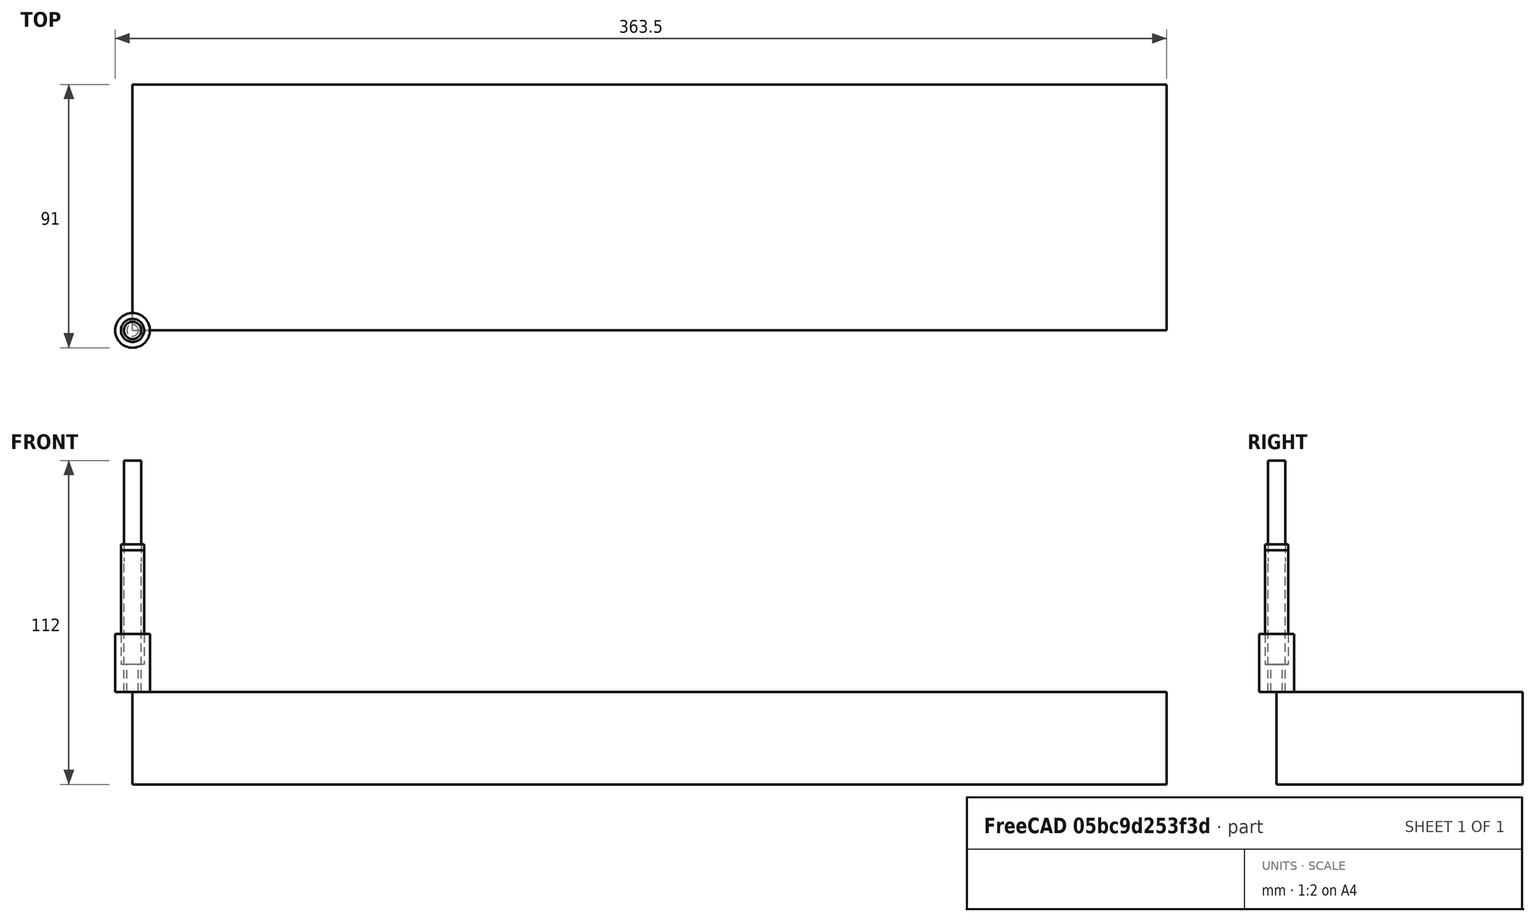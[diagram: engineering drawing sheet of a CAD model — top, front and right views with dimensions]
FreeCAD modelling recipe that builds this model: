
FCSTD DOCUMENT  (FreeCAD 0.22R34789 (Git))
Label: fence_side
License: All rights reserved
LicenseURL: http://en.wikipedia.org/wiki/All_rights_reserved
objects: Path::FeaturePython×8, Part::FeaturePython×5, Sketcher::SketchObject×4, PartDesign::Pocket×3, App::DocumentObjectGroup×3, PartDesign::Pad×1, PartDesign::Body×1, Spreadsheet::Sheet×1, App::FeaturePython×1, Mesh::FeaturePython×1
note: 21 computed .brp shape members not serialized (recipe doc carries the construction recipe); baked Part::Feature solids carry a one-line shape summary decoded from their .brp

FEATURE [Sketcher::SketchObject] Sketch012  label="fence_face"
  FullyConstrained = true
  MapMode = 5
  Support = -> [XY_Plane005]
  expr: .Constraints.fence_length = Spreadsheet.table_length / 2 - 45 / 2
  expr: Constraints[11] = 3 * Spreadsheet.table_radius
  sketch-geometry (6):
    g0: LineSegment StartX=18 StartY=65 StartZ=0 EndX=319.5 EndY=65 EndZ=0
    g1: LineSegment StartX=337.5 StartY=47 StartZ=0 EndX=337.5 EndY=0 EndZ=0
    g2: LineSegment StartX=337.5 StartY=0 StartZ=0 EndX=0 EndY=0 EndZ=0
    g3: LineSegment StartX=0 StartY=0 StartZ=0 EndX=0 EndY=47 EndZ=0
    g4: ArcOfCircle CenterX=18 CenterY=47 CenterZ=0 NormalX=0 NormalY=0 NormalZ=1 AngleXU=0 Radius=18 StartAngle=1.5708 EndAngle=3.14159
    g5: ArcOfCircle CenterX=319.5 CenterY=47 CenterZ=0 NormalX=0 NormalY=0 NormalZ=1 AngleXU=0 Radius=18 StartAngle=2e-16 EndAngle=1.5708
  constraints (15):
    c: Coincident(g1,g2)
    c: Coincident(g2,g3)
    c: Horizontal(g0)
    c: Horizontal(g2)
    c: Vertical(g1)
    c: Vertical(g3)
    c: Tangent(g3,g4) = 1.5708
    c: Tangent(g0,g4) = 1.5708
    c: Tangent(g0,g5) = 1.5708
    c: Tangent(g1,g5) = 1.5708
    c: Equal(g4,g5)
    c: Radius(g4) = 18
    c: DistanceX(g2,g2) = 337.5  'fence_length'
    c: Coincident(g2,g-1)
    c: DistanceY(g1,g0) = 65  'fence_height'
FEATURE [PartDesign::Pad] Pad005
  Direction = (0,0,1)
  Length = 32
  Length2 = 10
  Profile = -> Sketch012
  ReferenceAxis = -> Sketch012 [N_Axis]
  Type = 0
  expr: Length = Spreadsheet.fence_face_d
FEATURE [Sketcher::SketchObject] Sketch013
  FullyConstrained = true
  MapMode = 5
  Placement = pos=(0,0,32) rot=(0,0,1;0rad)
  Support = -> [Pad005]
  expr: Constraints[11] = Sketch012.Constraints.fence_height / 2 - 9.5 mm + 3 mm
  expr: Constraints[8] = Spreadsheet.t_track_width
  expr: Constraints[9] = Sketch012.Constraints.fence_length
  sketch-geometry (4):
    g0: LineSegment StartX=0 StartY=45 StartZ=0 EndX=337.5 EndY=45 EndZ=0
    g1: LineSegment StartX=337.5 StartY=45 StartZ=0 EndX=337.5 EndY=26 EndZ=0
    g2: LineSegment StartX=337.5 StartY=26 StartZ=0 EndX=0 EndY=26 EndZ=0
    g3: LineSegment StartX=0 StartY=26 StartZ=0 EndX=0 EndY=45 EndZ=0
  constraints (12):
    c: Coincident(g0,g1)
    c: Coincident(g1,g2)
    c: Coincident(g2,g3)
    c: Coincident(g3,g0)
    c: Horizontal(g0)
    c: Horizontal(g2)
    c: Vertical(g1)
    c: Vertical(g3)
    c: DistanceY(g3,g3) = 19
    c: DistanceX(g2,g2) = 337.5
    c: DistanceX(g2,g-1) = 0
    c: DistanceY(g-1,g2) = 26
FEATURE [PartDesign::Pocket] Pocket007
  BaseFeature = -> Pad005
  Direction = (0,0,-1)
  Length = 9.5
  Length2 = 5
  Profile = -> Sketch013
  ReferenceAxis = -> Sketch013 [N_Axis]
  Type = 0
  expr: Length = Spreadsheet.t_track_depth
FEATURE [Sketcher::SketchObject] Sketch014
  FullyConstrained = true
  MapMode = 5
  Placement = pos=(0,0,32) rot=(0,0,1;0rad)
  Support = -> [Pocket007]
  expr: Constraints[10] = Sketch012.Constraints.fence_length
  sketch-geometry (4):
    g0: LineSegment StartX=0 StartY=4 StartZ=0 EndX=337.5 EndY=4 EndZ=0
    g1: LineSegment StartX=337.5 StartY=4 StartZ=0 EndX=337.5 EndY=0 EndZ=0
    g2: LineSegment StartX=337.5 StartY=0 StartZ=0 EndX=0 EndY=0 EndZ=0
    g3: LineSegment StartX=0 StartY=0 StartZ=0 EndX=0 EndY=4 EndZ=0
  constraints (11):
    c: Coincident(g0,g1)
    c: Coincident(g1,g2)
    c: Coincident(g2,g3)
    c: Coincident(g3,g0)
    c: Horizontal(g0)
    c: Horizontal(g2)
    c: Vertical(g1)
    c: Vertical(g3)
    c: DistanceY(g1,g1) = 4
    c: Coincident(g2,g-1)
    c: DistanceX(g2,g2) = 337.5
FEATURE [PartDesign::Pocket] Pocket008
  BaseFeature = -> Pocket007
  Direction = (0,0,-1)
  Length = 4
  Length2 = 5
  Profile = -> Sketch014
  ReferenceAxis = -> Sketch014 [N_Axis]
  Type = 0
FEATURE [Sketcher::SketchObject] Sketch015
  FullyConstrained = true
  MapMode = 5
  Placement = pos=(0,0,0) rot=(1,0,0;3.14159rad)
  Support = -> [Pocket008]
  expr: Constraints[8] = Spreadsheet.fence_base_d
  expr: Constraints[9] = Sketch012.Constraints.fence_length
  sketch-geometry (4):
    g0: LineSegment StartX=0 StartY=0 StartZ=0 EndX=337.5 EndY=0 EndZ=0
    g1: LineSegment StartX=337.5 StartY=0 StartZ=0 EndX=337.5 EndY=-32 EndZ=0
    g2: LineSegment StartX=337.5 StartY=-32 StartZ=0 EndX=0 EndY=-32 EndZ=0
    g3: LineSegment StartX=0 StartY=-32 StartZ=0 EndX=0 EndY=0 EndZ=0
  constraints (11):
    c: Coincident(g0,g1)
    c: Coincident(g1,g2)
    c: Coincident(g2,g3)
    c: Coincident(g3,g0)
    c: Horizontal(g0)
    c: Horizontal(g2)
    c: Vertical(g1)
    c: Vertical(g3)
    c: DistanceY(g1,g1) = 32
    c: DistanceX(g0,g0) = 337.5
    c: Coincident(g-1,g0)
FEATURE [PartDesign::Pocket] Pocket009
  BaseFeature = -> Pocket008
  Direction = (0,0,1)
  Length = 6
  Length2 = 5
  Profile = -> Sketch015
  ReferenceAxis = -> Sketch015 [N_Axis]
  Type = 0
FEATURE [PartDesign::Body] Body004  label="fence_face_r"
  Group = -> [Sketch012,Pad005,Sketch013,Pocket007,Sketch014,Pocket008,Sketch015,Pocket009]
  Origin = -> Origin004
  Tip = -> Pocket009
FEATURE [Spreadsheet::Sheet] Spreadsheet
  cells = A1='table_length; B1(table_length)=720; D1='plywood_18; E1(ply_18)=18; F1='iron_cast_table; G1(iron_cast_table)=262; I1='nakrętka kłowa M8 DIN1624; L1='otwory_przelotowe; A2='table_depth; B2(table_depth)=420; D2='plywood_12; E2(ply_12)=12; F2='mounting_screws_distance; G2(mounting_screws_distance)=170; I2='M8_D; J2(DIN1624_M8_D)=22.2; L2='M8_D; M2(otw_przel_M8)=8.4; D3='plywood_3; E3(ply_3)=3; I3='M8_d1; J3(DIN1624_M8_d1)=9.1; A4='table_radius; B4(table_radius)=6; I4='M8_a; J4(DIN1624_M8_a)=1.2; I5='M8_L1; J5(DIN1624_M8_L1)=11; A6='t_track_slim_width; B6(t_track_width)=19; C6='https://allegro.pl/oferta/t-track-slim-1220mm-profil-aluminiowy-t-zielony-10608302634?fromVariant=12640372726; A7='t_track_slim_depth; B7(t_track_depth)=9.5; D7='fence_base_d; E7(fence_base_d)=32; I7='M10_D; J7(DIN1624_M10_D)=25.5; D8='fence_face_d; E8(fence_face_d)=32; I8='M10_d1; J8(DIN1624_M10_d1)=12; A9='clamp_slot_width; B9(clamp_slot_width)=32; I9='M10_a; J9(DIN1624_M10_a)=1.2; I10='M10_L1; J10(DIN1624_M10_L1)=13; A11='insert_width; B11(insert_width)=90; D11='base_width; E11(base_width)==G1; A12='insert_depth; B12(insert_depth)=200; D12='base_depth; E12(base_depth)==E1 + 60 + E2 + E15 + 10; I12='M12_D; J12(DIN1624_M12_D)=27; D13='base_height; E13(base_height)=75; I13='M12_d1; J13(DIN1624_M12_d1)=13.7; I14='M12_a; J14(DIN1624_M12_a)=1.6; D15='drawer_depth; E15(drawer_depth)=200; I15='M12_L1; J15(DIN1624_M12_L1)=14.5; D16='drawer_slide_width; E16=12.7; D17='drawer_total_depth; E17(drawer_total_depth)==E15 + 6; D18='drawer_total_width; E18(drawer_total_width)==E11 - 2 * E1 - 2 * E16; D19='drawer_total_height; E19(drawer_total_height)==E13 - E1 - 9
FEATURE [App::FeaturePython] SetupSheet  # Path/CAM operation (typed FeaturePython)
  ClearanceHeightExpression = OpStockZMax+SetupSheet.ClearanceHeightOffset
  ClearanceHeightOffset = 5
  CoolantMode = 0
  CoolantModes = None | Flood | Mist
  FinalDepthExpression = OpFinalDepth
  HorizRapid = 0
  SafeHeightExpression = OpStockZMax+SetupSheet.SafeHeightOffset
  SafeHeightOffset = 3
  StartDepthExpression = OpStartDepth
  StepDownExpression = OpToolDiameter
  VertRapid = 0
FEATURE [Part::FeaturePython] Clone  label="Model-fence_face_r"  # Draft clone (typed FeaturePython)
  AttacherType = Attacher::AttachEngine3D
  Fuse = false
  Objects = -> [Body004]
  PathResource = Model
  Placement = pos=(10,10,-32) rot=(1,0,0;0rad)
  Scale = (1,1,1)
FEATURE [App::DocumentObjectGroup] Model
  Group = -> [Clone]
FEATURE [Part::FeaturePython] Stock  # WARN: FeaturePython — macro-defined, semantics opaque (R4)
  Base = -> Model
  ExtXneg = 10
  ExtXpos = 10
  ExtYneg = 10
  ExtYpos = 10
  ExtZneg = 0
  ExtZpos = 0
  Placement = pos=(10,10,-32) rot=(0,0,1;0rad)
  StockType = FromBase
FEATURE [Part::FeaturePython] ToolBit001  label="6 mm endmill, D=6, H=45, L=80, S=6"  # Path/CAM toolbit (typed FeaturePython)
  BitPropertyNames = Chipload | CuttingEdgeHeight | Diameter | Flutes | Length | Material | ShankDiameter | SpindleDirection
  BitShape = <userpath>/.local/share/FreeCAD/Macro/Tools/Shape/endmill.fcstd
  Chipload = 0
  CuttingEdgeHeight = 45
  Diameter = 6
  File = <userpath>/.local/share/FreeCAD/Macro/Tools/Bit/03c10998-7ce6-11ee-8713-1065300da2fe.fctb
  Flutes = 2
  Length = 80
  Material = 1
  ShankDiameter = 6
  ShapeName = endmill
  SpindleDirection = 0
FEATURE [Path::FeaturePython] TC__6_mm_endmill__D_6__H_45__L_80__S_6  label="TC: 6 mm endmill, D=6, H=45, L=80, S=6"  # Path/CAM operation (typed FeaturePython)
  HorizFeed = 10
  HorizRapid = 0
  SpindleDir = 0
  SpindleSpeed = 0
  Tool = -> ToolBit001
  ToolNumber = 17
  VertFeed = 1
  VertRapid = 0
  expr: HorizRapid = SetupSheet.HorizRapid
  expr: VertRapid = SetupSheet.VertRapid
FEATURE [Part::FeaturePython] endmill_D_4__h_9_5__S_8  label="endmill D=4, h=9.5, S=8"  # Path/CAM toolbit (typed FeaturePython)
  BitPropertyNames = Chipload | CuttingEdgeHeight | Diameter | Flutes | Length | Material | ShankDiameter | SpindleDirection
  BitShape = <userpath>/.local/share/FreeCAD/Macro/Tools/Shape/endmill.fcstd
  Chipload = 0
  CuttingEdgeHeight = 9.5
  Diameter = 4
  File = <userpath>/.local/share/FreeCAD/Macro/Tools/Bit/3a316b3c-7fd7-11ee-b6a7-0242a6b4470b.fctb
  Flutes = 1
  Length = 49
  Material = 1
  ShankDiameter = 8
  ShapeName = endmill
  SpindleDirection = 0
FEATURE [Path::FeaturePython] TC__endmill_D_4__h_9_5__S_8  label="TC: endmill D=4, h=9.5, S=8"  # Path/CAM operation (typed FeaturePython)
  HorizFeed = 10
  HorizRapid = 0
  SpindleDir = 0
  SpindleSpeed = 0
  Tool = -> endmill_D_4__h_9_5__S_8
  ToolNumber = 18
  VertFeed = 1
  VertRapid = 0
  expr: HorizRapid = SetupSheet.HorizRapid
  expr: VertRapid = SetupSheet.VertRapid
FEATURE [Path::FeaturePython] Slot  # Path/CAM operation (typed FeaturePython)
  Active = true
  Base = -> [Clone]
  ClearanceHeight = 5
  CoolantMode = 0
  CustomPoint1 = (353.5,12,0)
  CustomPoint2 = (4,12,0)
  CutPattern = 1
  CycleTime = 00:02:08
  ExtendPathEnd = 6
  ExtendPathStart = 6
  ExtendRadius = 0
  FinalDepth = -4
  LayerMode = 1
  OpFinalDepth = -4
  OpStartDepth = 0
  OpStockZMax = 0
  OpStockZMin = -32
  OpToolDiameter = 4
  PathOrientation = 0
  Reference1 = 0
  Reference2 = 0
  ReverseDirection = false
  SafeHeight = 3
  ShowTempObjects = false
  StartDepth = 0
  StartPoint = (0,0,0)
  StepDown = 2
  ToolController = -> TC__endmill_D_4__h_9_5__S_8
  UseStartPoint = false
  expr: ClearanceHeight = OpStockZMax + SetupSheet.ClearanceHeightOffset
  expr: FinalDepth = OpFinalDepth
  expr: SafeHeight = OpStockZMax + SetupSheet.SafeHeightOffset
  expr: StartDepth = OpStartDepth
  expr: StepDown = OpToolDiameter / 2
FEATURE [Part::FeaturePython] ToolBit  label="endmill D=12, H=20, S=8"  # Path/CAM toolbit (typed FeaturePython)
  BitPropertyNames = Chipload | CuttingEdgeHeight | Diameter | Flutes | Length | Material | ShankDiameter | SpindleDirection
  BitShape = <userpath>/.local/share/FreeCAD/Macro/Tools/Shape/endmill.fcstd
  Chipload = 0
  CuttingEdgeHeight = 20
  Diameter = 12
  File = <userpath>/.local/share/FreeCAD/Macro/Tools/Bit/d4c3dad8-7323-11ee-af98-1065300da2fe.fctb
  Flutes = 2
  Length = 51
  Material = 0
  ShankDiameter = 8
  ShapeName = endmill
  SpindleDirection = 0
FEATURE [Path::FeaturePython] TC__endmill_D_12__H_20__S_8  label="TC: endmill D=12, H=20, S=8"  # Path/CAM operation (typed FeaturePython)
  HorizFeed = 10
  HorizRapid = 0
  SpindleDir = 0
  SpindleSpeed = 0
  Tool = -> ToolBit
  ToolNumber = 14
  VertFeed = 1
  VertRapid = 0
  expr: HorizRapid = SetupSheet.HorizRapid
  expr: VertRapid = SetupSheet.VertRapid
FEATURE [App::DocumentObjectGroup] Tools
  Group = -> [TC__6_mm_endmill__D_6__H_45__L_80__S_6,TC__endmill_D_4__h_9_5__S_8,TC__endmill_D_12__H_20__S_8]
FEATURE [Path::FeaturePython] Pocket_Shape  # Path/CAM operation (typed FeaturePython)
  Active = true
  AreaParams:
    Tolerance = 1e-07
    FitArcs = True
    Simplify = False
    CleanDistance = 0.0
    Accuracy = 0.01
    Unit = 1.0
    MinArcPoints = 4
    MaxArcPoints = 100
    ClipperScale = 10000000.0
    Fill = 0
    Coplanar = 0
    Reorient = True
    Outline = False
    Explode = False
    OpenMode = 0
    Deflection = 0.01
    SubjectFill = 0
    ClipFill = 0
    Offset = 0.0
    ExtraPass = 0
    Stepover = 0.0
    LastStepover = 0.0
    JoinType = 0
    EndType = 0
    MiterLimit = 2.0
    RoundPrecision = 0.0
    PocketMode = 2
    ToolRadius = 6.0
    PocketExtraOffset = -0.75
    PocketStepover = 9.600000000000001
    PocketLastStepover = 0.0
    FromCenter = True
    Angle = 45.0
    AngleShift = 0.0
    Shift = 0.0
    Thicken = False
    SectionCount = -1
    Stepdown = 1.0
    SectionOffset = 0.0
    SectionTolerance = 1e-07
    SectionMode = 2
    Project = False
  Base = -> [Clone]
  ClearanceHeight = 5
  CoolantMode = 0
  CutMode = 0
  CycleTime = 00:17:14
  ExtensionCorners = true
  ExtensionFeature = -> [Clone]
  ExtensionLengthDefault = 6
  ExtraOffset = -0.75
  FinalDepth = -10.4
  FinishDepth = 0
  KeepToolDown = false
  MinTravel = false
  OffsetPattern = 1
  OpFinalDepth = -9.5
  OpStartDepth = 0
  OpStockZMax = 0
  OpStockZMin = -32
  OpToolDiameter = 12
  PathParams = {'orientation': 1, 'feedrate': 10.0, 'feedrate_v': 1.0, 'verbose': True, 'resume_height': 3.0, 'retraction': 5.0, 'return_end': True, 'preamble': False}
  PocketLastStepOver = 0
  SafeHeight = 3
  SplitArcs = false
  StartAt = 0
  StartDepth = 0
  StartPoint = (0,0,0)
  StepDown = 2
  StepOver = 80
  ToolController = -> TC__endmill_D_12__H_20__S_8
  UseOutline = false
  UseRestMachining = false
  UseStartPoint = false
  ZigZagAngle = 45
  expr: ClearanceHeight = OpStockZMax + SetupSheet.ClearanceHeightOffset
  expr: ExtensionLengthDefault = OpToolDiameter / 2
  expr: FinalDepth = OpFinalDepth - 0.9 mm
  expr: SafeHeight = OpStockZMax + SetupSheet.SafeHeightOffset
  expr: StartDepth = OpStartDepth
  expr: StepDown = OpToolDiameter / 6
FEATURE [Path::FeaturePython] Profile  # Path/CAM operation (typed FeaturePython)
  Active = true
  AreaParams:
    Tolerance = 1e-07
    FitArcs = True
    Simplify = False
    CleanDistance = 0.0
    Accuracy = 0.01
    Unit = 1.0
    MinArcPoints = 4
    MaxArcPoints = 100
    ClipperScale = 10000000.0
    Fill = 0
    Coplanar = 0
    Reorient = True
    Outline = False
    Explode = False
    OpenMode = 0
    Deflection = 0.01
    SubjectFill = 0
    ClipFill = 0
    Offset = 3.0
    ExtraPass = 0
    Stepover = 0.0
    LastStepover = 0.0
    JoinType = 0
    EndType = 0
    MiterLimit = 2.0
    RoundPrecision = 0.0
    PocketMode = 0
    ToolRadius = 1.0
    PocketExtraOffset = 0.0
    PocketStepover = 0.0
    PocketLastStepover = 0.0
    FromCenter = False
    Angle = 45.0
    AngleShift = 0.0
    Shift = 0.0
    Thicken = False
    SectionCount = -1
    Stepdown = 1.0
    SectionOffset = 0.0
    SectionTolerance = 1e-07
    SectionMode = 2
    Project = False
  ClearanceHeight = 5
  CoolantMode = 0
  CycleTime = 00:24:14
  Direction = 0
  FinalDepth = -34
  HandleMultipleFeatures = 0
  JoinType = 0
  MiterLimit = 0.1
  OffsetExtra = 0
  OpFinalDepth = -32
  OpStartDepth = 0
  OpStockZMax = 0
  OpStockZMin = -32
  OpToolDiameter = 6
  PathParams = {'orientation': 1, 'feedrate': 10.0, 'feedrate_v': 1.0, 'verbose': True, 'resume_height': 3.0, 'retraction': 5.0, 'return_end': True, 'preamble': False}
  SafeHeight = 3
  Side = 0
  SplitArcs = false
  StartDepth = 0
  StartPoint = (0,0,0)
  StepDown = 2
  ToolController = -> TC__6_mm_endmill__D_6__H_45__L_80__S_6
  UseComp = true
  UseStartPoint = false
  processCircles = false
  processHoles = false
  processPerimeter = true
  expr: ClearanceHeight = OpStockZMax + SetupSheet.ClearanceHeightOffset
  expr: FinalDepth = OpFinalDepth - 2 mm
  expr: SafeHeight = OpStockZMax + SetupSheet.SafeHeightOffset
  expr: StartDepth = OpStartDepth
  expr: StepDown = OpToolDiameter / 3
FEATURE [Path::FeaturePython] DressupTag  # Path/CAM operation (typed FeaturePython)
  Angle = 45
  Base = -> Profile
  Height = 8
  Positions = (4) [(263.125,7,0),(94.375,7,0),(103.301,77.9988,0),(254.1,77.9996,0)]
  Radius = 0
  SegmentationFactor = 50
  Width = 14
FEATURE [App::DocumentObjectGroup] Operations
  Group = -> [Slot,Pocket_Shape,DressupTag]
FEATURE [Path::FeaturePython] Job  # Path/CAM operation (typed FeaturePython)
  CycleTime = 00:43:36
  Fixtures = G54
  GeometryTolerance = 0.01
  JobType = 0
  Model = -> Model
  Operations = -> Operations
  OrderOutputBy = 1
  PostProcessor = 3
  PostProcessorOutputFile = %D/%d.gcode
  SetupSheet = -> SetupSheet
  SplitOutput = true
  Stock = -> Stock
  Tools = -> Tools
FEATURE [Mesh::FeaturePython] CutMaterial001  # WARN: FeaturePython — macro-defined, semantics opaque (R4)
